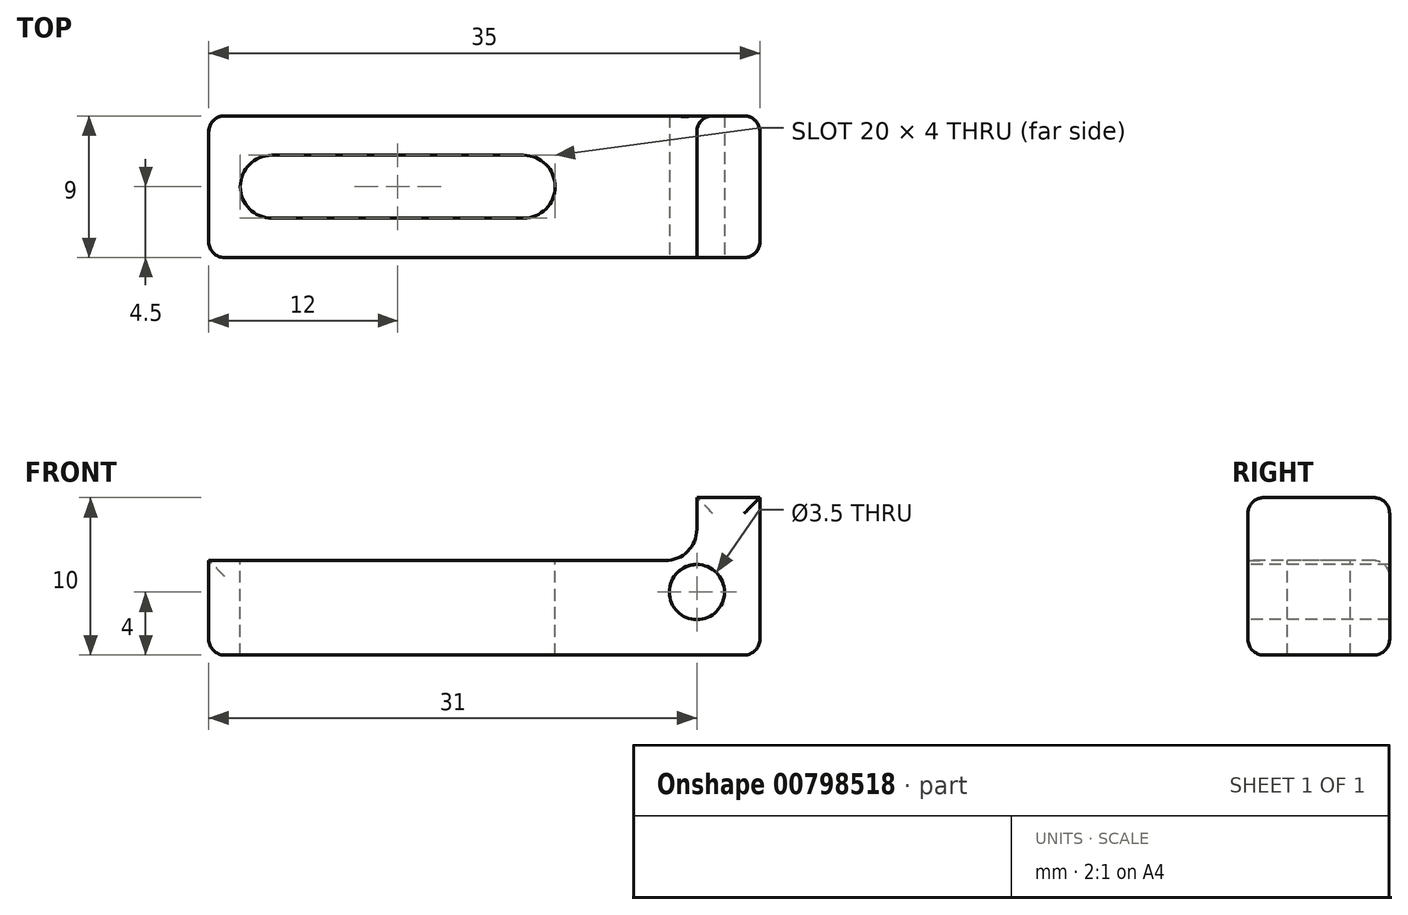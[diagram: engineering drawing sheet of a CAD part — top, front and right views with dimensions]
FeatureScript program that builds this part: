
annotation { "Feature Type Name" : "Feature", "Feature Type Description" : "" }
export const myFeature = defineFeature(function(context is Context, id is Id, definition is map)
    precondition{}
    {
        {
            var Q0;
            Q0=qCreatedBy(makeId("Top.planeOp"),FACE);
            var sketch = newSketch(context, id + "F0", { "sketchPlane" : qUnion([Q0])});
            skLineSegment(sketch, "E0.bottom", {"start": v(17.5, -4.5) * mm, "end": v(-17.5, -4.5) * mm});
            skLineSegment(sketch, "E0.top", {"start": v(17.5, 4.5) * mm, "end": v(-17.5, 4.5) * mm});
            skLineSegment(sketch, "E0.left", {"start": v(17.5, -4.5) * mm, "end": v(17.5, 4.5) * mm});
            skLineSegment(sketch, "E0.right", {"start": v(-17.5, -4.5) * mm, "end": v(-17.5, 4.5) * mm});
            skPoint(sketch, "E0.middle", {"position": v(0, 0) * mm});
            skSolve(sketch);
        }
        {
            var Q0;
            Q0 = qSketchRegion(id + "F0", true);
            extrude(context, id + "F1", {"entities" : qUnion([Q0]), "depth" : 10 * mm, "offsetDistance" : 25 * mm});
        }
        {
            var Q0;
            Q0=makeQuery(id+"F1.opExtrude","SWEPT_FACE",FACE,{"disambiguationData":[OSD([sQuery(id+"F0.wireOp",EDGE,"E0.bottom")])]});
            var sketch = newSketch(context, id + "F2", { "sketchPlane" : qUnion([Q0])});
            skLineSegment(sketch, "E1.bottom", {"start": v(-17.5, 10) * mm, "end": v(13.5, 10) * mm});
            skLineSegment(sketch, "E1.top", {"start": v(-17.5, 6) * mm, "end": v(11.5, 6) * mm});
            skLineSegment(sketch, "E1.left", {"start": v(-17.5, 10) * mm, "end": v(-17.5, 6) * mm});
            skLineSegment(sketch, "E1.right", {"start": v(13.5, 10) * mm, "end": v(13.5, 8) * mm});
            skLineSegment(sketch, "E2", {"start": v(17.5, 0) * mm, "end": v(13.5, 0) * mm, "construction": true});
            skLineSegment(sketch, "E3", {"start": v(13.5, 0) * mm, "end": v(13.5, 4) * mm, "construction": true});
            skCircle(sketch, "E4", {"center": v(13.5, 4) * mm, "radius": 1.75 * mm});
            skPoint(sketch, "E5.visualSharp", {"position": v(13.5, 6) * mm});
            skArc(sketch, "E5.filletArc", {"start": v(11.5, 6) * mm, "mid": v(12.91, 6.59) * mm, "end": v(13.5, 8) * mm});
            skSolve(sketch);
        }
        {
            var Q0;
            Q0=makeQuery(id+"F2.imprint","IMPRINT",FACE,{"disambiguationData":[TD([[makeQuery(id+"F2.imprint","IMPRINT",EDGE,{"derivedFrom":sQuery(id+"F2.wireOp",EDGE,"E1.bottom")}),1.0]])]});
            var Q1;
            Q1=makeQuery(id+"F2.imprint","IMPRINT",FACE,{"disambiguationData":[TD([[makeQuery(id+"F2.imprint","IMPRINT",EDGE,{"derivedFrom":sQuery(id+"F2.wireOp",EDGE,"E4")}),1.0]])]});
            extrude(context, id + "F3", {"entities" : qUnion([Q0, Q1]), "operationType" : NewBodyOperationType.REMOVE, "endBound" : BoundingType.THROUGH_ALL, "oppositeDirection" : true, "depth" : 25 * mm, "offsetDistance" : 25 * mm});
        }
        {
            var Q0;
            Q0=makeQuery(id+"F3.boolean.opBoolean","COPY",FACE,{"derivedFrom":makeQuery(id+"F3.opExtrude","SWEPT_FACE",FACE,{"disambiguationData":[OSD([sQuery(id+"F2.wireOp",EDGE,"E1.top")])]})});
            var sketch = newSketch(context, id + "F4", { "sketchPlane" : qUnion([Q0])});
            skLineSegment(sketch, "E6", {"start": v(-17.5, 0) * mm, "end": v(-13.5, 0) * mm, "construction": true});
            skLineSegment(sketch, "E7", {"start": v(-13.5, 0) * mm, "end": v(2.5, 0) * mm, "construction": true});
            skCircle(sketch, "E8", {"center": v(-13.5, 0) * mm, "radius": 2 * mm});
            skCircle(sketch, "E9", {"center": v(2.5, 0) * mm, "radius": 2 * mm});
            skLineSegment(sketch, "E10", {"start": v(-13.5, 2) * mm, "end": v(2.5, 2) * mm});
            skLineSegment(sketch, "E11", {"start": v(-13.5, -2) * mm, "end": v(2.5, -2) * mm});
            skSolve(sketch);
        }
        {
            var Q0;
            {var subQ0=sQuery(id+"F4.wireOp",EDGE,"E8");var subQ1=makeQuery(id+"F4.imprint","INTERSECT",VERTEX,{"derivedFrom":[subQ0,sQuery(id+"F4.wireOp",EDGE,"E10")]});Q0=makeQuery(id+"F4.imprint","IMPRINT",FACE,{"disambiguationData":[TD([[makeQuery(id+"F4.imprint","IMPRINT",EDGE,{"disambiguationData":[TD([[subQ1,-1.0]])],"derivedFrom":subQ0}),1.0]])]});}
            var Q1;
            {var subQ0=sQuery(id+"F4.wireOp",EDGE,"E10");Q1=makeQuery(id+"F4.imprint","IMPRINT",FACE,{"disambiguationData":[TD([[makeQuery(id+"F4.imprint","IMPRINT",EDGE,{"derivedFrom":subQ0}),-1.0]])]});}
            var Q2;
            {var subQ0=sQuery(id+"F4.wireOp",EDGE,"E9");var subQ1=makeQuery(id+"F4.imprint","INTERSECT",VERTEX,{"derivedFrom":[subQ0,sQuery(id+"F4.wireOp",EDGE,"E10")]});Q2=makeQuery(id+"F4.imprint","IMPRINT",FACE,{"disambiguationData":[TD([[makeQuery(id+"F4.imprint","IMPRINT",EDGE,{"disambiguationData":[TD([[subQ1,-1.0]])],"derivedFrom":subQ0}),1.0]])]});}
            extrude(context, id + "F5", {"entities" : qUnion([Q0, Q1, Q2]), "operationType" : NewBodyOperationType.REMOVE, "endBound" : BoundingType.THROUGH_ALL, "oppositeDirection" : true, "depth" : 25 * mm, "offsetDistance" : 25 * mm});
        }
        {
            var Q0;
            Q0=makeQuery(id+"F3.boolean.opBoolean","COPY",EDGE,{"derivedFrom":makeQuery(id+"F3.opExtrude","CAP_EDGE",EDGE,{"disambiguationData":[OSD([sQuery(id+"F2.wireOp",EDGE,"E1.top")])],"isStart":true})});
            var Q1;
            Q1=makeQuery(id+"F3.boolean.opBoolean","COPY",EDGE,{"derivedFrom":makeQuery(id+"F3.opExtrude","SWEPT_EDGE",EDGE,{"disambiguationData":[OSD([sQuery(id+"F0.wireOp",EDGE,"E0.bottom"),sQuery(id+"F0.wireOp",EDGE,"E0.right"),sQuery(id+"F2.wireOp",EDGE,"E1.top"),sQuery(id+"F2.wireOp",EDGE,"E1.left")])]})});
            var Q2;
            Q2=makeQuery(id+"F3.boolean.opBoolean","INTERSECT",EDGE,{"derivedFrom":[makeQuery(id+"F1.opExtrude","SWEPT_FACE",FACE,{"disambiguationData":[OSD([sQuery(id+"F0.wireOp",EDGE,"E0.top")])]}),makeQuery(id+"F3.opExtrude","SWEPT_FACE",FACE,{"disambiguationData":[OSD([sQuery(id+"F2.wireOp",EDGE,"E1.top")])]})]});
            var Q3;
            Q3=makeQuery(id+"F1.opExtrude","CAP_EDGE",EDGE,{"disambiguationData":[OSD([sQuery(id+"F0.wireOp",EDGE,"E0.bottom")])],"isStart":false});
            var Q4;
            Q4=makeQuery(id+"F1.opExtrude","CAP_EDGE",EDGE,{"disambiguationData":[OSD([sQuery(id+"F0.wireOp",EDGE,"E0.top")])],"isStart":false});
            var Q5;
            Q5=makeQuery(id+"F1.opExtrude","CAP_EDGE",EDGE,{"disambiguationData":[OSD([sQuery(id+"F0.wireOp",EDGE,"E0.bottom")])],"isStart":true});
            var Q6;
            Q6=makeQuery(id+"F1.opExtrude","SWEPT_EDGE",EDGE,{"disambiguationData":[OSD([sQuery(id+"F0.wireOp",EDGE,"E0.bottom"),sQuery(id+"F0.wireOp",EDGE,"E0.right")])]});
            var Q7;
            Q7=makeQuery(id+"F1.opExtrude","CAP_EDGE",EDGE,{"disambiguationData":[OSD([sQuery(id+"F0.wireOp",EDGE,"E0.right")])],"isStart":true});
            var Q8;
            Q8=makeQuery(id+"F1.opExtrude","SWEPT_EDGE",EDGE,{"disambiguationData":[OSD([sQuery(id+"F0.wireOp",EDGE,"E0.top"),sQuery(id+"F0.wireOp",EDGE,"E0.right")])]});
            var Q9;
            Q9=makeQuery(id+"F1.opExtrude","CAP_EDGE",EDGE,{"disambiguationData":[OSD([sQuery(id+"F0.wireOp",EDGE,"E0.top")])],"isStart":true});
            var Q10;
            Q10=makeQuery(id+"F1.opExtrude","CAP_EDGE",EDGE,{"disambiguationData":[OSD([sQuery(id+"F0.wireOp",EDGE,"E0.left")])],"isStart":true});
            var Q11;
            Q11=makeQuery(id+"F1.opExtrude","SWEPT_EDGE",EDGE,{"disambiguationData":[OSD([sQuery(id+"F0.wireOp",EDGE,"E0.top"),sQuery(id+"F0.wireOp",EDGE,"E0.left")])]});
            var Q12;
            Q12=makeQuery(id+"F1.opExtrude","SWEPT_EDGE",EDGE,{"disambiguationData":[OSD([sQuery(id+"F0.wireOp",EDGE,"E0.bottom"),sQuery(id+"F0.wireOp",EDGE,"E0.left")])]});
            fillet(context, id + "F6", {"entities" : qUnion([Q0, Q1, Q2, Q3, Q4, Q5, Q6, Q7, Q8, Q9, Q10, Q11, Q12]), "radius" : 1 * mm, "tangentPropagation" : true, "allowEdgeOverflow" : false});
        }
    });
